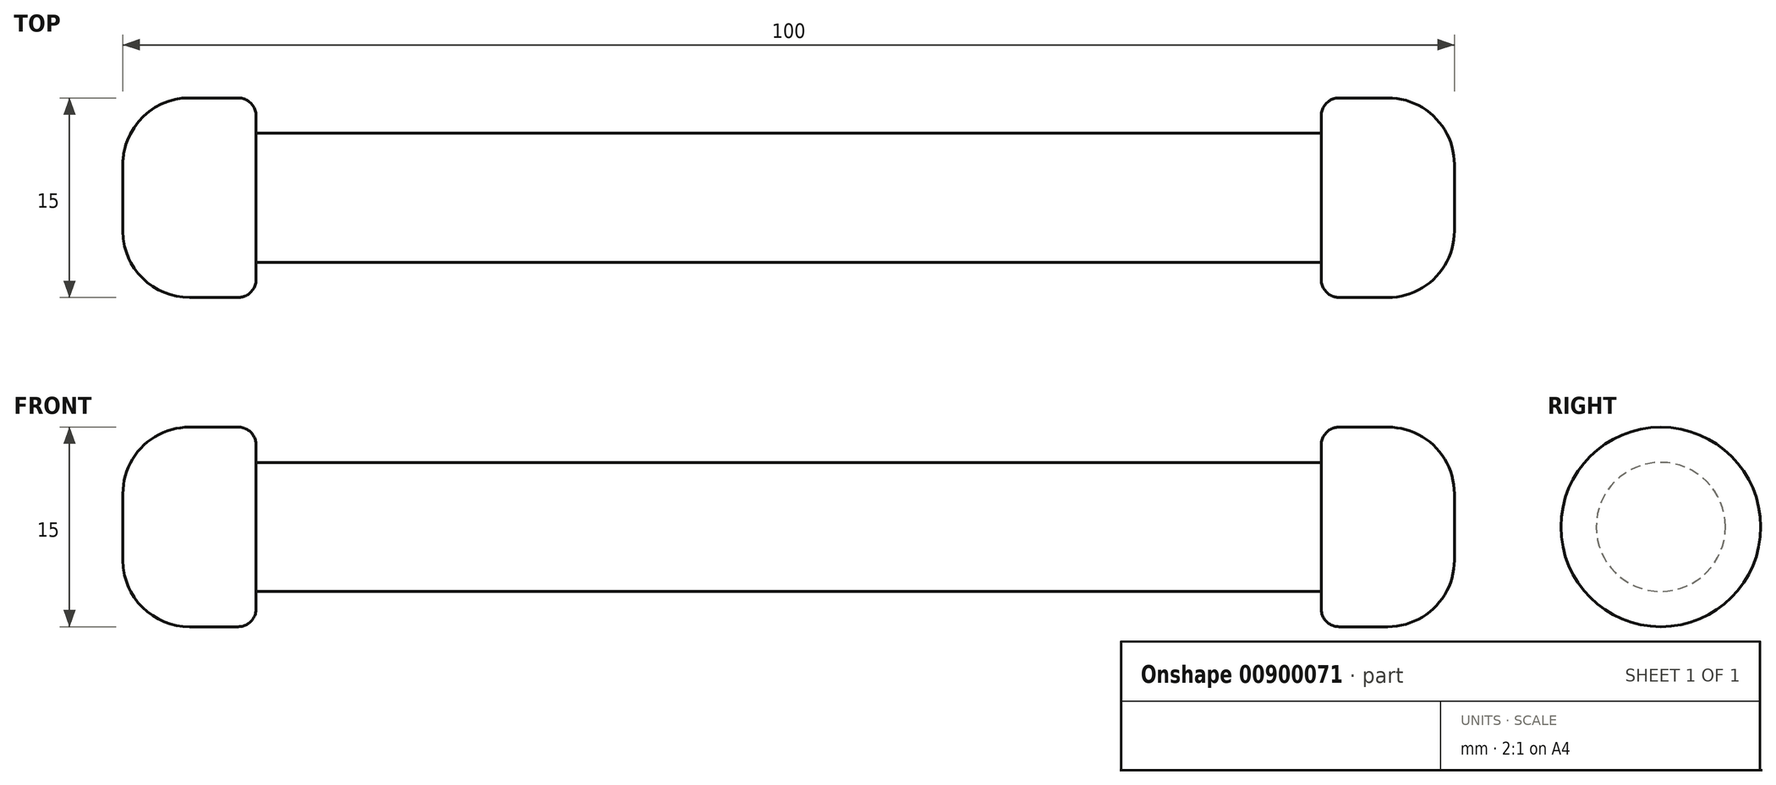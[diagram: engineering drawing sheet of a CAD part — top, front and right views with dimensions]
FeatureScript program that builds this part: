
annotation { "Feature Type Name" : "Feature", "Feature Type Description" : "" }
export const myFeature = defineFeature(function(context is Context, id is Id, definition is map)
    precondition{}
    {
        {
            var Q0;
            Q0=qCreatedBy(makeId("Right.planeOp"),FACE);
            var sketch = newSketch(context, id + "F0", { "sketchPlane" : qUnion([Q0])});
            skCircle(sketch, "E0", {"center": v(0, 0) * mm, "radius": 4.85 * mm});
            skSolve(sketch);
        }
        {
            var Q0;
            Q0 = qSketchRegion(id + "F0", true);
            extrude(context, id + "F1", {"entities" : qUnion([Q0]), "depth" : 80 * mm, "offsetDistance" : 25 * mm});
        }
        {
            var Q0;
            Q0=makeQuery(id+"F1.opExtrude","CAP_FACE",FACE,{"disambiguationData":[OSD([sQuery(id+"F0.wireOp",EDGE,"E0")])],"isStart":false});
            var sketch = newSketch(context, id + "F2", { "sketchPlane" : qUnion([Q0])});
            skCircle(sketch, "E1", {"center": v(0, 0) * mm, "radius": 7.5 * mm});
            skSolve(sketch);
        }
        {
            var Q0;
            Q0 = qSketchRegion(id + "F2", true);
            extrude(context, id + "F3", {"entities" : qUnion([Q0]), "operationType" : NewBodyOperationType.ADD, "depth" : 10 * mm, "offsetDistance" : 25 * mm});
        }
        {
            var Q0;
            Q0=makeQuery(id+"F1.opExtrude","CAP_FACE",FACE,{"disambiguationData":[OSD([sQuery(id+"F0.wireOp",EDGE,"E0")])],"isStart":true});
            var sketch = newSketch(context, id + "F4", { "sketchPlane" : qUnion([Q0])});
            skCircle(sketch, "E2", {"center": v(0, 0) * mm, "radius": 7.5 * mm});
            skSolve(sketch);
        }
        {
            var Q0;
            Q0 = qSketchRegion(id + "F4", true);
            extrude(context, id + "F5", {"entities" : qUnion([Q0]), "operationType" : NewBodyOperationType.ADD, "depth" : 10 * mm, "offsetDistance" : 25 * mm});
        }
        {
            var Q0;
            Q0=makeQuery(id+"F1.opExtrude","CAP_EDGE",EDGE,{"disambiguationData":[OSD([sQuery(id+"F0.wireOp",EDGE,"E0")])],"isStart":true});
            var Q1;
            Q1=makeQuery(id+"F5.opExtrude","CAP_EDGE",EDGE,{"disambiguationData":[OSD([sQuery(id+"F4.wireOp",EDGE,"E2")])],"isStart":true});
            fillet(context, id + "F6", {"entities" : qUnion([Q0, Q1]), "radius" : 1.32 * mm, "tangentPropagation" : true, "allowEdgeOverflow" : false});
        }
        {
            var Q0;
            Q0=makeQuery(id+"F1.opExtrude","CAP_EDGE",EDGE,{"disambiguationData":[OSD([sQuery(id+"F0.wireOp",EDGE,"E0")])],"isStart":false});
            var Q1;
            Q1=makeQuery(id+"F3.opExtrude","CAP_EDGE",EDGE,{"disambiguationData":[OSD([sQuery(id+"F2.wireOp",EDGE,"E1")])],"isStart":true});
            fillet(context, id + "F7", {"entities" : qUnion([Q0, Q1]), "radius" : 1.32 * mm, "tangentPropagation" : true, "allowEdgeOverflow" : false});
        }
        {
            var Q0;
            Q0=makeQuery(id+"F5.opExtrude","CAP_EDGE",EDGE,{"disambiguationData":[OSD([sQuery(id+"F4.wireOp",EDGE,"E2")])],"isStart":false});
            var Q1;
            Q1=makeQuery(id+"F3.opExtrude","CAP_EDGE",EDGE,{"disambiguationData":[OSD([sQuery(id+"F2.wireOp",EDGE,"E1")])],"isStart":false});
            fillet(context, id + "F8", {"entities" : qUnion([Q0, Q1]), "radius" : 5 * mm, "tangentPropagation" : true, "allowEdgeOverflow" : false});
        }
    });
